FREECAD ASSEMBLY — COMPONENT RECIPES ("Assembly_WireFlexureUnit")

This assembly document has 16 components, labeled P0..P15 below (a component is one placed body or linked part). 5 of them carry a construction recipe — the FreeCAD feature program that regenerates the part from scratch, quoted from this document or its linked companion documents; the rest are supplied as boundary geometry only. No exploded tour is included for this assembly.
COMPONENT P0 — geometry summary ("Ball1"; no construction recipe available for this part):
  bounding box: 1.5 x 1.4 x 1.4 mm
  tessellated surface: 2,124 triangles
  volume: 2 mm^3 (51% of its bounding box)
  symmetry: revolution-symmetric about the x axis through its bounding-box center; 2-fold rotationally symmetric about the y axis; 2-fold rotationally symmetric about the z axis; mirror-symmetric across its y mid-plane
COMPONENT P1 — geometry summary ("Ball2"; no construction recipe available for this part):
  bounding box: 1.5 x 1.4 x 1.4 mm
  tessellated surface: 2,124 triangles
  volume: 2 mm^3 (51% of its bounding box)
  symmetry: revolution-symmetric about the x axis through its bounding-box center; 2-fold rotationally symmetric about the y axis; 2-fold rotationally symmetric about the z axis; mirror-symmetric across its y mid-plane
COMPONENT P2 — geometry summary ("Ball3"; no construction recipe available for this part):
  bounding box: 1.5 x 1.4 x 1.4 mm
  tessellated surface: 2,124 triangles
  volume: 2 mm^3 (51% of its bounding box)
  symmetry: revolution-symmetric about the x axis through its bounding-box center; 2-fold rotationally symmetric about the y axis; 2-fold rotationally symmetric about the z axis; mirror-symmetric across its y mid-plane
COMPONENT P3 — geometry summary ("Ball4"; no construction recipe available for this part):
  bounding box: 1.5 x 1.4 x 1.4 mm
  tessellated surface: 2,124 triangles
  volume: 2 mm^3 (51% of its bounding box)
  symmetry: revolution-symmetric about the x axis through its bounding-box center; 2-fold rotationally symmetric about the y axis; 2-fold rotationally symmetric about the z axis; mirror-symmetric across its y mid-plane
COMPONENT P4 — geometry summary ("FlexureWire1"; no construction recipe available for this part):
  bounding box: 72.0 x 2.0 x 2.0 mm
  tessellated surface: 2,260 triangles
  volume: 224 mm^3 (78% of its bounding box)
  symmetry: 2-fold rotationally symmetric about the x axis; revolution-symmetric about the y axis through its bounding-box center; 2-fold rotationally symmetric about the z axis; mirror-symmetric across its x mid-plane, y mid-plane, z mid-plane
COMPONENT P5 — geometry summary ("FlexureWire2"; no construction recipe available for this part):
  bounding box: 72.0 x 2.0 x 2.0 mm
  tessellated surface: 2,260 triangles
  volume: 224 mm^3 (78% of its bounding box)
  symmetry: 2-fold rotationally symmetric about the x axis; revolution-symmetric about the y axis through its bounding-box center; 2-fold rotationally symmetric about the z axis; mirror-symmetric across its x mid-plane, y mid-plane, z mid-plane
COMPONENT P6 — geometry summary ("RubberBand"; no construction recipe available for this part):
  bounding box: 22.2 x 4.5 x 1.0 mm
  tessellated surface: 13,932 triangles
  volume: 36 mm^3 (36% of its bounding box)
  symmetry: 2-fold rotationally symmetric about the y axis; mirror-symmetric across its z mid-plane
COMPONENT P7 — recipe-attached ("RubberBand001", a linked part whose construction recipe lives in a companion FreeCAD document of the same project; that document's serialized recipe follows).
Construction recipe (the companion document, serialized — sketch geometry with constraints, then the solid features built on it; lengths are millimeters unless a unit is written):

FCSTD DOCUMENT  (FreeCAD 1.1R41365 (Git))
Label: RubberBand
License: All rights reserved
LicenseURL: https://en.wikipedia.org/wiki/All_rights_reserved
objects: Sketcher::SketchObject×2, App::Point×1, PartDesign::AdditivePipe×1, PartDesign::Mirrored×1, PartDesign::Body×1
note: 10 computed .brp shape members not serialized (recipe doc carries the construction recipe); baked Part::Feature solids carry a one-line shape summary decoded from their .brp

FEATURE [App::Point] Origin001
  Role = Origin
FEATURE [Sketcher::SketchObject] Sketch
  ArcFitTolerance = 1e-06
  AttachmentSupport = -> [Origin]
  ExternalTypes = [0]
  FullyConstrained = true
  MakeInternals = false
  MapMode = 5
  sketch-geometry (2):
    g0: LineSegment StartX=-1.75 StartY=0 StartZ=0 EndX=-1.75 EndY=20 EndZ=0
    g1: ArcOfCircle CenterX=0 CenterY=20 CenterZ=0 NormalX=0 NormalY=0 NormalZ=1 AngleXU=0 Radius=1.75 StartAngle=1.5708 EndAngle=3.14159
  constraints (7):
    c: PointOnObject(g0,g-1)
    c: Vertical(g0)
    c: PointOnObject(g1,g-2)
    c: PointOnObject(g1,g-2)
    c: Tangent(g1,g0) = 1.5708
    c: Distance(g-1,g0) = 1.75
    c: DistanceY(g0,g0) = 20
FEATURE [Sketcher::SketchObject] Sketch001
  ArcFitTolerance = 1e-06
  AttachmentSupport = -> [Origin]
  ExternalGeometry = -> [Sketch]
  ExternalTypes = [0]
  FullyConstrained = true
  MakeInternals = false
  MapMode = 5
  Placement = pos=(0,0,0) rot=(1,0,0;1.5708rad)
  sketch-geometry (1):
    g0: Circle CenterX=-1.75 CenterY=0 CenterZ=0 NormalX=0 NormalY=0 NormalZ=1 AngleXU=0 Radius=0.5
  constraints (2):
    c: Diameter(g0) = 1
    c: Coincident(g0,g-3)
FEATURE [PartDesign::AdditivePipe] AdditivePipe
  AuxiliaryCurvilinear = true
  AuxiliarySpineTangent = false
  Binormal = (0,0,0)
  Mode = 0
  Profile = -> Sketch001
  Refine = true
  Spine = -> Sketch
  SpineTangent = false
  Suppressed = false
  Transformation = 0
  Transition = 0
FEATURE [PartDesign::Mirrored] Mirrored
  BaseFeature = -> AdditivePipe
  MirrorPlane = -> YZ_Plane
  Refine = true
  Suppressed = false
  TransformMode = 1
FEATURE [PartDesign::Body] Body  label="RubberBand"
  AllowCompound = false
  Group = -> [Sketch,Sketch001,AdditivePipe,Mirrored]
  Origin = -> Origin
  Tip = -> Mirrored
COMPONENT P8 — same part as P7; its construction recipe is shown at P7.
COMPONENT P9 — same part as P7; its construction recipe is shown at P7.
COMPONENT P10 — geometry summary ("RubberBandCollet"; no construction recipe available for this part):
  bounding box: 5.9 x 4.0 x 3.0 mm
  tessellated surface: 2,496 triangles
  volume: 43 mm^3 (60% of its bounding box)
  symmetry: 2-fold rotationally symmetric about the x axis; 2-fold rotationally symmetric about the y axis; 2-fold rotationally symmetric about the z axis; mirror-symmetric across its y mid-plane, z mid-plane
COMPONENT P11 — geometry summary ("RubberBandCollet001"; no construction recipe available for this part):
  bounding box: 5.9 x 4.0 x 3.0 mm
  tessellated surface: 2,496 triangles
  volume: 43 mm^3 (60% of its bounding box)
  symmetry: 2-fold rotationally symmetric about the x axis; 2-fold rotationally symmetric about the y axis; 2-fold rotationally symmetric about the z axis; mirror-symmetric across its y mid-plane, z mid-plane
COMPONENT P12 — geometry summary ("RubberBandCollet002"; no construction recipe available for this part):
  bounding box: 5.9 x 4.0 x 3.0 mm
  tessellated surface: 2,496 triangles
  volume: 43 mm^3 (60% of its bounding box)
  symmetry: 2-fold rotationally symmetric about the x axis; 2-fold rotationally symmetric about the y axis; 2-fold rotationally symmetric about the z axis; mirror-symmetric across its y mid-plane, z mid-plane
COMPONENT P13 — geometry summary ("RubberBandCollet003"; no construction recipe available for this part):
  bounding box: 5.9 x 4.0 x 3.0 mm
  tessellated surface: 2,496 triangles
  volume: 43 mm^3 (60% of its bounding box)
  symmetry: 2-fold rotationally symmetric about the x axis; 2-fold rotationally symmetric about the y axis; 2-fold rotationally symmetric about the z axis; mirror-symmetric across its y mid-plane, z mid-plane
COMPONENT P14 — recipe-attached ("WireMount1", a linked part whose construction recipe lives in a companion FreeCAD document of the same project; that document's serialized recipe follows).
Construction recipe (the companion document, serialized — sketch geometry with constraints, then the solid features built on it; lengths are millimeters unless a unit is written):

FCSTD DOCUMENT  (FreeCAD 1.1R41365 (Git))
Label: BallJointMount
License: All rights reserved
LicenseURL: https://en.wikipedia.org/wiki/All_rights_reserved
objects: Sketcher::SketchObject×4, PartDesign::Pocket×3, PartDesign::Chamfer×2, App::Point×1, PartDesign::Pad×1, PartDesign::Fillet×1, PartDesign::Mirrored×1, PartDesign::Body×1
note: 32 computed .brp shape members not serialized (recipe doc carries the construction recipe); baked Part::Feature solids carry a one-line shape summary decoded from their .brp

FEATURE [App::Point] Origin001
  Role = Origin
FEATURE [Sketcher::SketchObject] Sketch
  ArcFitTolerance = 1e-06
  AttachmentSupport = -> [XY_Plane]
  ExternalTypes = [0]
  FullyConstrained = true
  MakeInternals = false
  MapMode = 5
  sketch-geometry (5):
    g0: LineSegment StartX=-10 StartY=-3 StartZ=0 EndX=0 EndY=-3 EndZ=0
    g1: LineSegment StartX=0 StartY=-3 StartZ=0 EndX=0 EndY=3 EndZ=0
    g2: LineSegment StartX=0 StartY=3 StartZ=0 EndX=-10 EndY=3 EndZ=0
    g3: GeomPoint [constr] X=0 Y=0 Z=0
    g4: LineSegment StartX=-10 StartY=3 StartZ=0 EndX=-10 EndY=-3 EndZ=0
  constraints (12):
    c: Coincident(g0,g1)
    c: Coincident(g1,g2)
    c: Horizontal(g0)
    c: Horizontal(g2)
    c: Vertical(g1)
    c: Coincident(g3,g-1)
    c: DistanceX(g0,g0) = 10
    c: DistanceY(g1,g1) = 6
    c: Symmetric(g1,g1,g3)
    c: Coincident(g4,g2)
    c: Coincident(g4,g0)
    c: Vertical(g4)
FEATURE [PartDesign::Pad] Pad
  Direction = (0,0,1)
  Length = 6
  Length2 = 10
  Midplane = true
  Profile = -> Sketch
  ReferenceAxis = -> Sketch [N_Axis]
  Refine = true
  Suppressed = false
  Type = 0
FEATURE [Sketcher::SketchObject] Sketch001
  ArcFitTolerance = 1e-06
  AttachmentSupport = -> [Pad]
  ExternalTypes = [0]
  FullyConstrained = true
  MakeInternals = false
  MapMode = 5
  Placement = pos=(0,0,3) rot=(0,0,1;0rad)
  sketch-geometry (1):
    g0: Circle CenterX=-5 CenterY=0 CenterZ=0 NormalX=0 NormalY=0 NormalZ=1 AngleXU=0 Radius=1.1
  constraints (3):
    c: Diameter(g0) = 2.2
    c: DistanceX(g0,g-1) = 5
    c: PointOnObject(g0,g-1)
FEATURE [PartDesign::Pocket] Pocket
  BaseFeature = -> Pad
  Direction = (0,0,-1)
  Length = 5
  Length2 = 5
  Profile = -> Sketch001
  ReferenceAxis = -> Sketch001 [N_Axis]
  Refine = true
  Suppressed = false
  Type = 1
FEATURE [Sketcher::SketchObject] Sketch002
  ArcFitTolerance = 1e-06
  AttachmentSupport = -> [Pocket]
  ExternalTypes = [0]
  FullyConstrained = true
  MakeInternals = false
  MapMode = 5
  Placement = pos=(0,-3,0) rot=(1,0,0;1.5708rad)
  sketch-geometry (1):
    g0: Circle CenterX=-8.5 CenterY=0 CenterZ=0 NormalX=0 NormalY=0 NormalZ=1 AngleXU=0 Radius=0.5
  constraints (3):
    c: Diameter(g0) = 1
    c: DistanceX(g0,g-1) = 8.5
    c: PointOnObject(g0,g-1)
FEATURE [PartDesign::Pocket] Pocket001
  BaseFeature = -> Pocket
  Direction = (0,1,-2e-16)
  Length = 1
  Length2 = 5
  Profile = -> Sketch002
  ReferenceAxis = -> Sketch002 [N_Axis]
  Refine = true
  Suppressed = false
  Type = 0
FEATURE [PartDesign::Chamfer] Chamfer
  Angle = 45
  Base = -> Pocket001 [Edge14]
  BaseFeature = -> Pocket001
  ChamferType = 0
  FlipDirection = false
  Refine = true
  Size = 1.2
  Size2 = 1
  SupportTransform = false
  Suppressed = false
  UseAllEdges = false
FEATURE [Sketcher::SketchObject] Sketch004
  ArcFitTolerance = 1e-06
  AttachmentSupport = -> [Chamfer]
  ExternalGeometry = -> [Chamfer]
  ExternalTypes = [0]
  FullyConstrained = true
  MakeInternals = false
  MapMode = 5
  Placement = pos=(0,-3,0) rot=(1,0,0;1.5708rad)
  sketch-geometry (3):
    g0: Circle CenterX=-8.5 CenterY=1.75 CenterZ=0 NormalX=0 NormalY=0 NormalZ=1 AngleXU=0 Radius=0.6
    g1: Circle CenterX=-8.5 CenterY=-1.75 CenterZ=0 NormalX=0 NormalY=0 NormalZ=1 AngleXU=0 Radius=0.6
    g2: LineSegment [constr] StartX=-8.5 StartY=1.75 StartZ=0 EndX=-8.5 EndY=-1.75 EndZ=0
  constraints (7):
    c: Diameter(g0) = 1.2
    c: Equal(g0,g1)
    c: Coincident(g2,g0)
    c: Coincident(g2,g1)
    c: Symmetric(g2,g2,g-3)
    c: Distance(g2,g2) = 3.5
    c: Vertical(g2)
FEATURE [PartDesign::Pocket] Pocket002
  BaseFeature = -> Chamfer
  Direction = (0,1,-2e-16)
  Length = 5
  Length2 = 5
  Profile = -> Sketch004
  ReferenceAxis = -> Sketch004 [N_Axis]
  Refine = true
  Suppressed = false
  Type = 1
FEATURE [PartDesign::Fillet] Fillet
  Base = -> Pocket002 [Edge3,Edge15]
  BaseFeature = -> Pocket002
  Radius = 0.5
  Refine = true
  SupportTransform = false
  Suppressed = false
  UseAllEdges = false
FEATURE [PartDesign::Mirrored] Mirrored
  BaseFeature = -> Fillet
  MirrorPlane = -> YZ_Plane
  Refine = true
  Suppressed = false
  TransformMode = 1
FEATURE [PartDesign::Chamfer] Chamfer001
  Angle = 45
  Base = -> Mirrored [Edge5,Edge11]
  BaseFeature = -> Mirrored
  ChamferType = 0
  FlipDirection = false
  Refine = true
  Size = 0.2
  Size2 = 1
  SupportTransform = false
  Suppressed = false
  UseAllEdges = false
FEATURE [PartDesign::Body] Body  label="BallJointMount"
  AllowCompound = false
  Group = -> [Sketch,Pad,Sketch001,Pocket,Sketch002,Pocket001,Chamfer,Sketch004,Pocket002,Fillet,Mirrored,Chamfer001]
  Origin = -> Origin
  Tip = -> Chamfer001
COMPONENT P15 — same part as P14; its construction recipe is shown at P14.
PROVENANCE & LICENSES
A FreeCAD (.FCStd) document from a public repository crawl; recipes are the document's own serialized feature recipes (and, for linked parts, companion documents' recipes).
License: mit.
